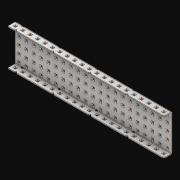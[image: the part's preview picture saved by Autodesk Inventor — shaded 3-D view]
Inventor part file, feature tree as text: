
AUTODESK INVENTOR PART (.ipt)
format: ipt  version: 2021 (Build 250183000, 183)  size: 3,453,440 bytes
history: native  units: in
note: dims shown in document units (in); Inventor stores cm internally (conversion verified against a paired STEP export)
features: extrude x148, other x147, sketch x4, thicken_offset x3, pattern_linear x3, imported_body x1
ambient origin geometry x8: Origin, YZ Plane, XZ Plane, XY Plane, X Axis, Y Axis, Z Axis, Center Point
bodies: Solid1 (feature_tree)
feature tree (306):
  thicken_offset  "Thicken1"
  thicken_offset  "Thicken2"
  thicken_offset  "Thicken3"
  pattern_linear  "Rectangular Pattern1"  Spacing1=0.001in  [1 undecoded]
  pattern_linear  "Rectangular Pattern2"  Spacing1=0.001in  [1 undecoded]
  pattern_linear  "Rectangular Pattern3"  Spacing1=0.182in  [1 undecoded]
  extrude  "Extrusion1"  Depth=0.063in TaperAngle=0.0deg
  sketch  "Sketch1"  dims[d0=0.001in]
  other  "Srf1"
  sketch  "Sketch2"  dims[d1=0.001in]
  other  "Srf2"
  sketch  "Sketch3"  dims[d2=0.001in]
  other  "Srf3"
  other  "Srf4"
  other  "Srf5"
  other  "Srf6"
  other  "Srf7"
  other  "Srf8"
  other  "Srf9"
  other  "Srf10"
  other  "Srf11"
  other  "Srf12"
  other  "Srf13"
  other  "Srf14"
  other  "Srf15"
  other  "Srf16"
  other  "Srf17"
  other  "Srf18"
  other  "Srf19"
  other  "Srf20"
  other  "Srf21"
  other  "Srf22"
  other  "Srf23"
  other  "Srf38"
  other  "Srf39"
  other  "Srf40"
  other  "Srf41"
  other  "Srf42"
  other  "Srf43"
  other  "Srf44"
  other  "Srf45"
  other  "Srf46"
  other  "Srf47"
  other  "Srf48"
  other  "Srf49"
  other  "Srf50"
  other  "Srf51"
  other  "Srf52"
  other  "Srf53"
  other  "Srf54"
  other  "Srf55"
  other  "Srf56"
  other  "Srf57"
  other  "Srf72"
  other  "Srf73"
  other  "Srf74"
  other  "Srf75"
  other  "Srf76"
  other  "Srf77"
  other  "Srf78"
  other  "Srf79"
  other  "Srf80"
  other  "Srf81"
  other  "Srf82"
  other  "Srf83"
  other  "Srf84"
  other  "Srf85"
  other  "Srf86"
  other  "Srf87"
  other  "Srf88"
  other  "Srf89"
  other  "Srf90"
  other  "Srf91"
  other  "Srf106"
  other  "Srf107"
  other  "Srf108"
  other  "Srf109"
  other  "Srf110"
  other  "Srf111"
  other  "Srf112"
  other  "Srf113"
  other  "Srf114"
  other  "Srf115"
  other  "Srf116"
  other  "Srf117"
  other  "Srf118"
  other  "Srf119"
  other  "Srf120"
  other  "Srf121"
  other  "Srf122"
  other  "Srf123"
  other  "Srf124"
  other  "Srf125"
  other  "Srf126"
  other  "Srf141"
  other  "Srf142"
  other  "Srf143"
  other  "Srf144"
  other  "Srf145"
  other  "Srf146"
  other  "Srf147"
  other  "Srf148"
  other  "Srf149"
  other  "Srf150"
  other  "Srf151"
  other  "Srf152"
  other  "Srf153"
  other  "Srf154"
  other  "Srf155"
  other  "Srf156"
  other  "Srf157"
  other  "Srf158"
  other  "Srf159"
  other  "Srf160"
  other  "Srf161"
  other  "Srf176"
  other  "Srf177"
  other  "Srf178"
  other  "Srf179"
  other  "Srf180"
  other  "Srf181"
  other  "Srf182"
  other  "Srf183"
  other  "Srf184"
  other  "Srf185"
  other  "Srf186"
  other  "Srf187"
  other  "Srf188"
  other  "Srf189"
  other  "Srf190"
  other  "Srf191"
  other  "Srf192"
  other  "Srf193"
  other  "Srf194"
  other  "Srf195"
  other  "Srf196"
  other  "Srf211"
  other  "Srf212"
  other  "Srf213"
  other  "Srf214"
  other  "Srf215"
  other  "Srf216"
  other  "Srf217"
  other  "Srf218"
  other  "Srf219"
  other  "Srf220"
  other  "Srf221"
  other  "Srf222"
  other  "Srf223"
  other  "Srf224"
  other  "Srf225"
  other  "Srf226"
  other  "Srf227"
  other  "Srf228"
  other  "Srf229"
  other  "Srf230"
  other  "Srf231"
  sketch  "Sketch4"  dims[d3=0.001in d4=0.001in d5=0.001in d6=0.182in d7=0.063in d8=0.0in d9=0.182in d10=0.063in d11=0.0in d12=0.182in d13=0.063in d14=0.0in d17=0.5in d18=8.2677in d20=0.5in d21=8.2677in d23=0.5in d24=1.9685in d26=0.5in d27=7.0in d28=0.0in]
  imported_body  "Imported1"
  extrude  "ExtrusionSrf1"  Depth=7.0in
  extrude  "ExtrusionSrf2"  Depth=0.063in TaperAngle=0.0deg
  extrude  "ExtrusionSrf3"  Depth=7.0in
  extrude  "ExtrusionSrf4"  Depth=0.063in TaperAngle=0.0deg
  extrude  "ExtrusionSrf5"  Depth=0.5in
  extrude  "ExtrusionSrf6"  Depth=7.0in
  extrude  "ExtrusionSrf7"  Depth=0.5in
  extrude  "ExtrusionSrf8"  Depth=7.0in
  extrude  "ExtrusionSrf9"  Depth=0.5in
  extrude  "ExtrusionSrf10"  Depth=0.5in
  extrude  "ExtrusionSrf11"  Depth=7.0in
  extrude  "ExtrusionSrf12"  TaperAngle=0.0deg  [1 undecoded]
  extrude  "ExtrusionSrf13"  [1 undecoded]
  extrude  "ExtrusionSrf14"  [1 undecoded]
  extrude  "ExtrusionSrf15"  [1 undecoded]
  extrude  "ExtrusionSrf16"  [1 undecoded]
  extrude  "ExtrusionSrf17"  [1 undecoded]
  extrude  "ExtrusionSrf18"  [1 undecoded]
  extrude  "ExtrusionSrf19"  [1 undecoded]
  extrude  "ExtrusionSrf20"  [1 undecoded]
  extrude  "ExtrusionSrf21"  [1 undecoded]
  extrude  "ExtrusionSrf22"  [1 undecoded]
  extrude  "ExtrusionSrf23"  [1 undecoded]
  extrude  "ExtrusionSrf38"  [1 undecoded]
  extrude  "ExtrusionSrf39"  [1 undecoded]
  extrude  "ExtrusionSrf40"  [1 undecoded]
  extrude  "ExtrusionSrf41"  [1 undecoded]
  extrude  "ExtrusionSrf42"  [1 undecoded]
  extrude  "ExtrusionSrf43"  [1 undecoded]
  extrude  "ExtrusionSrf44"  [1 undecoded]
  extrude  "ExtrusionSrf45"  [1 undecoded]
  extrude  "ExtrusionSrf46"  [1 undecoded]
  extrude  "ExtrusionSrf47"  [1 undecoded]
  extrude  "ExtrusionSrf48"  [1 undecoded]
  extrude  "ExtrusionSrf49"  [1 undecoded]
  extrude  "ExtrusionSrf50"  [1 undecoded]
  extrude  "ExtrusionSrf51"  [1 undecoded]
  extrude  "ExtrusionSrf52"  [1 undecoded]
  extrude  "ExtrusionSrf53"  [1 undecoded]
  extrude  "ExtrusionSrf54"  [1 undecoded]
  extrude  "ExtrusionSrf55"  [1 undecoded]
  extrude  "ExtrusionSrf56"  [1 undecoded]
  extrude  "ExtrusionSrf57"  [1 undecoded]
  extrude  "ExtrusionSrf72"  [1 undecoded]
  extrude  "ExtrusionSrf73"  [1 undecoded]
  extrude  "ExtrusionSrf74"  [1 undecoded]
  extrude  "ExtrusionSrf75"  [1 undecoded]
  extrude  "ExtrusionSrf76"  [1 undecoded]
  extrude  "ExtrusionSrf77"  [1 undecoded]
  extrude  "ExtrusionSrf78"  [1 undecoded]
  extrude  "ExtrusionSrf79"  [1 undecoded]
  extrude  "ExtrusionSrf80"  [1 undecoded]
  extrude  "ExtrusionSrf81"  [1 undecoded]
  extrude  "ExtrusionSrf82"  [1 undecoded]
  extrude  "ExtrusionSrf83"  [1 undecoded]
  extrude  "ExtrusionSrf84"  [1 undecoded]
  extrude  "ExtrusionSrf85"  [1 undecoded]
  extrude  "ExtrusionSrf86"  [1 undecoded]
  extrude  "ExtrusionSrf87"  [1 undecoded]
  extrude  "ExtrusionSrf88"  [1 undecoded]
  extrude  "ExtrusionSrf89"  [1 undecoded]
  extrude  "ExtrusionSrf90"  [1 undecoded]
  extrude  "ExtrusionSrf91"  [1 undecoded]
  extrude  "ExtrusionSrf106"  [1 undecoded]
  extrude  "ExtrusionSrf107"  [1 undecoded]
  extrude  "ExtrusionSrf108"  [1 undecoded]
  extrude  "ExtrusionSrf109"  [1 undecoded]
  extrude  "ExtrusionSrf110"  [1 undecoded]
  extrude  "ExtrusionSrf111"  [1 undecoded]
  extrude  "ExtrusionSrf112"  [1 undecoded]
  extrude  "ExtrusionSrf113"  [1 undecoded]
  extrude  "ExtrusionSrf114"  [1 undecoded]
  extrude  "ExtrusionSrf115"  [1 undecoded]
  extrude  "ExtrusionSrf116"  [1 undecoded]
  extrude  "ExtrusionSrf117"  [1 undecoded]
  extrude  "ExtrusionSrf118"  [1 undecoded]
  extrude  "ExtrusionSrf119"  [1 undecoded]
  extrude  "ExtrusionSrf120"  [1 undecoded]
  extrude  "ExtrusionSrf121"  [1 undecoded]
  extrude  "ExtrusionSrf122"  [1 undecoded]
  extrude  "ExtrusionSrf123"  [1 undecoded]
  extrude  "ExtrusionSrf124"  [1 undecoded]
  extrude  "ExtrusionSrf125"  [1 undecoded]
  extrude  "ExtrusionSrf126"  [1 undecoded]
  extrude  "ExtrusionSrf141"  [1 undecoded]
  extrude  "ExtrusionSrf142"  [1 undecoded]
  extrude  "ExtrusionSrf143"  [1 undecoded]
  extrude  "ExtrusionSrf144"  [1 undecoded]
  extrude  "ExtrusionSrf145"  [1 undecoded]
  extrude  "ExtrusionSrf146"  [1 undecoded]
  extrude  "ExtrusionSrf147"  [1 undecoded]
  extrude  "ExtrusionSrf148"  [1 undecoded]
  extrude  "ExtrusionSrf149"  [1 undecoded]
  extrude  "ExtrusionSrf150"  [1 undecoded]
  extrude  "ExtrusionSrf151"  [1 undecoded]
  extrude  "ExtrusionSrf152"  [1 undecoded]
  extrude  "ExtrusionSrf153"  [1 undecoded]
  extrude  "ExtrusionSrf154"  [1 undecoded]
  extrude  "ExtrusionSrf155"  [1 undecoded]
  extrude  "ExtrusionSrf156"  [1 undecoded]
  extrude  "ExtrusionSrf157"  [1 undecoded]
  extrude  "ExtrusionSrf158"  [1 undecoded]
  extrude  "ExtrusionSrf159"  [1 undecoded]
  extrude  "ExtrusionSrf160"  [1 undecoded]
  extrude  "ExtrusionSrf161"  [1 undecoded]
  extrude  "ExtrusionSrf176"  [1 undecoded]
  extrude  "ExtrusionSrf177"  [1 undecoded]
  extrude  "ExtrusionSrf178"  [1 undecoded]
  extrude  "ExtrusionSrf179"  [1 undecoded]
  extrude  "ExtrusionSrf180"  [1 undecoded]
  extrude  "ExtrusionSrf181"  [1 undecoded]
  extrude  "ExtrusionSrf182"  [1 undecoded]
  extrude  "ExtrusionSrf183"  [1 undecoded]
  extrude  "ExtrusionSrf184"  [1 undecoded]
  extrude  "ExtrusionSrf185"  [1 undecoded]
  extrude  "ExtrusionSrf186"  [1 undecoded]
  extrude  "ExtrusionSrf187"  [1 undecoded]
  extrude  "ExtrusionSrf188"  [1 undecoded]
  extrude  "ExtrusionSrf189"  [1 undecoded]
  extrude  "ExtrusionSrf190"  [1 undecoded]
  extrude  "ExtrusionSrf191"  [1 undecoded]
  extrude  "ExtrusionSrf192"  [1 undecoded]
  extrude  "ExtrusionSrf193"  [1 undecoded]
  extrude  "ExtrusionSrf194"  [1 undecoded]
  extrude  "ExtrusionSrf195"  [1 undecoded]
  extrude  "ExtrusionSrf196"  [1 undecoded]
  extrude  "ExtrusionSrf211"  [1 undecoded]
  extrude  "ExtrusionSrf212"  [1 undecoded]
  extrude  "ExtrusionSrf213"  [1 undecoded]
  extrude  "ExtrusionSrf214"  [1 undecoded]
  extrude  "ExtrusionSrf215"  [1 undecoded]
  extrude  "ExtrusionSrf216"  [1 undecoded]
  extrude  "ExtrusionSrf217"  [1 undecoded]
  extrude  "ExtrusionSrf218"  [1 undecoded]
  extrude  "ExtrusionSrf219"  [1 undecoded]
  extrude  "ExtrusionSrf220"  [1 undecoded]
  extrude  "ExtrusionSrf221"  [1 undecoded]
  extrude  "ExtrusionSrf222"  [1 undecoded]
  extrude  "ExtrusionSrf223"  [1 undecoded]
  extrude  "ExtrusionSrf224"  [1 undecoded]
  extrude  "ExtrusionSrf225"  [1 undecoded]
  extrude  "ExtrusionSrf226"  [1 undecoded]
  extrude  "ExtrusionSrf227"  [1 undecoded]
  extrude  "ExtrusionSrf228"  [1 undecoded]
  extrude  "ExtrusionSrf229"  [1 undecoded]
  extrude  "ExtrusionSrf230"  [1 undecoded]
  extrude  "ExtrusionSrf231"  [1 undecoded]
note: 139 required parameter values undecoded (feature->parameter linkage not recoverable at this tier; creation-order binding heuristic only, values carry confidence <= 0.55)
